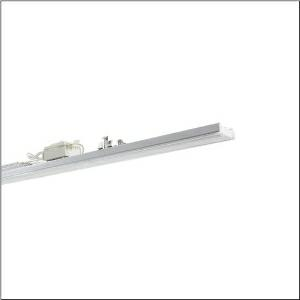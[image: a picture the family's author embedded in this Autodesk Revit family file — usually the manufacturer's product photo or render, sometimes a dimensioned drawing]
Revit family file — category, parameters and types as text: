
# Revit family: licross_11_recessed_mo_51tl197n485g
name_source: partatom
category: Lighting Fixtures
units: mm (PartAtom-declared; Revit-internal decimal feet)

## family parameters
Cut with Voids When Loaded = No
Host = Face
Light Source = No
Part Type = Normal
Room Calculation Point = No
Round Connector Dimension = Use Diameter
Shared = No

## types (1)
- Licross 11 Recessed MO (1 x LED, 8580 lm, 48.5 W, 4000K)
    Apparent Load = 49 VA
    CIE Flux Codes = 55 90 98 100 100
    Color Rendering = 80
    Color Temperature = 4000K
    Default Elevation = 1800 mm
    Description = Licross 11 Recessed MO, luminaire insert, of sheet steel, coil coated, white, length: 1.500mm, width: 66mm, height: 67mm, LED rated luminous flux: 8.580lm, light colour: 840, SDCM (Standard Deviation of Colour Matching)MacAdam ≤ 2 SDCM (initial), control gear: ON/OFF, with plug, 3-pole, with phase selection, mains connection: 220..240V, AC, 50/60Hz, rated input power: 49W, internal wiring halogen-free, primary light control with lens, of plastic, primary optical cover: cover, of PMMA, light emission: direct distribution, primary light characteristic: double asymmetric, protection rating (complete): IP40, insulation class (complete): insulation class I (protective earthing), certification: CE, ENEC, VDE, UKCA, protection symbol: D if used in an environment without relevant dust loads with corresponding accessories, impact resistance: IK06, permissible ambient temperature for indoor applications: -35..+35°C, corresponds to IFS (International Featured Standards) requirements for safety and quality in the food industry, reducing of maximum allowable ambient temperature of 5°C with ceiling mounting, The light source and the operating device comply with the requirements of the Ecodesign Regulation (EU) 2019/2020 and are replaceable in accordance with this regulation, packaging unit: 1 piece
    Height = 58 mm
    Lamp = 1 x LED
    Lamp Light Flux = 8580 lm
    Lamp Power = 48.5 W
    Lamp count = 1
    Length = 1500 mm
    Luminous efficacy = 177 lm/W
    Manufacturer = Siteco
    ModVariant = No
    Model = 51TL197N485G
    Mounting Place = Ceiling
    Mounting Type = Pendant
    Number of Poles = 1
    OnlyDefault = Yes
    Power Factor = 1
    Product Name = Licross 11 Recessed MO
    Product group = luminaire insert | ceiling pendant
    ProductGroupID = 901
    Protection Class = Protection class I
    Protection Degree = IP 40
    RLX_Detail_Level = 1
    RLX_Emergency_Light_Flux = 0 lm
    RLX_Emergency_Type = 0
    RLX_Emergency_Type_DB = No
    RlxData = <blob elided: 21101 chars, md5=2f12e177>
    Socket = socket
    Standby Power = 0 W
    System Light Flux = 8580 lm
    System Power = 49 W
    Type Comments = Product without accessories
    Type Image = l_1296930.jpg
    URL = http://relux.com
    VarID = ---
    Voltage = 0 V
    Weight = 0.00 kg
    Width = 66 mm

## geometry (parser evidence)
native form markers: Blend x4, Sweep x10
no freeform markers — native parametric forms only
